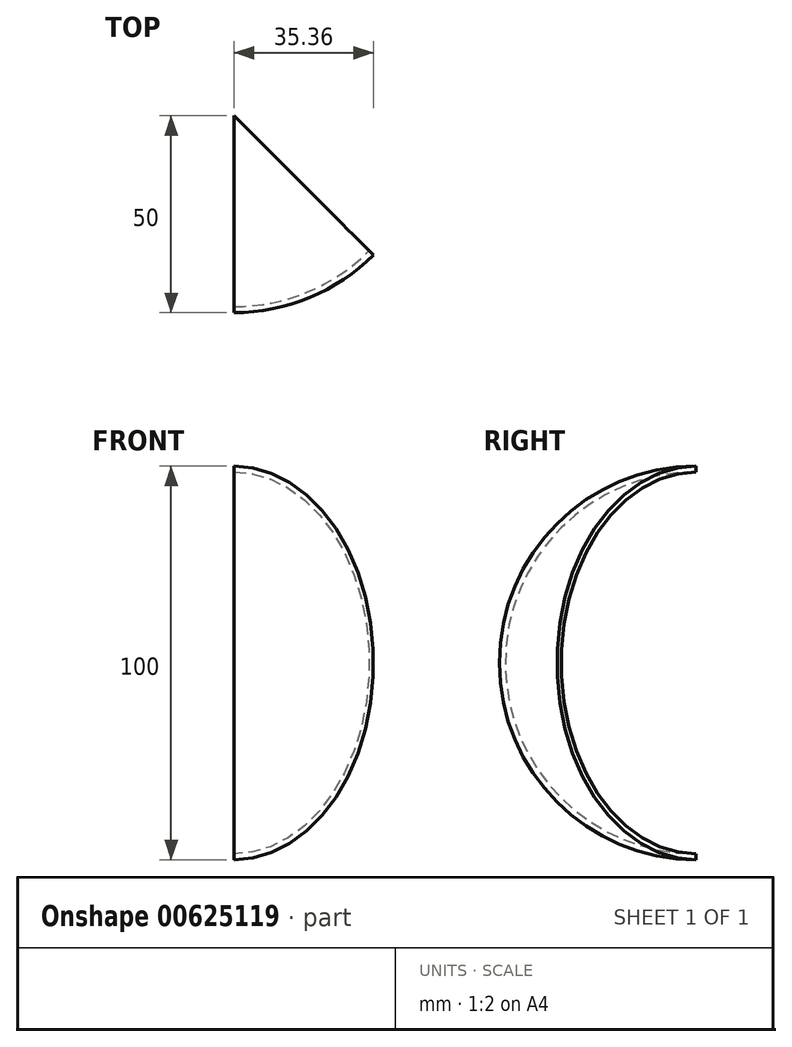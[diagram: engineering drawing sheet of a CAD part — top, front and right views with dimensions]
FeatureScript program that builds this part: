
annotation { "Feature Type Name" : "Feature", "Feature Type Description" : "" }
export const myFeature = defineFeature(function(context is Context, id is Id, definition is map)
    precondition{}
    {
        {
            var Q0;
            Q0=qCreatedBy(makeId("Front.planeOp"),FACE);
            var sketch = newSketch(context, id + "F0", { "sketchPlane" : qUnion([Q0])});
            skArc(sketch, "E0", {"start": v(0, -50) * mm, "mid": v(50, 0) * mm, "end": v(0, 50) * mm});
            skArc(sketch, "E1", {"start": v(0, -48.5) * mm, "mid": v(48.5, 0) * mm, "end": v(0, 48.5) * mm});
            skLineSegment(sketch, "E2", {"start": v(0, 50) * mm, "end": v(0, -50) * mm});
            skSolve(sketch);
        }
        {
            var Q0;
            {var subQ0=sQuery(id+"F0.wireOp",EDGE,"E0");Q0=makeQuery(id+"F0.imprint","IMPRINT",FACE,{"disambiguationData":[TD([[makeQuery(id+"F0.imprint","IMPRINT",EDGE,{"derivedFrom":subQ0}),1.0]])]});}
            var Q1;
            Q1=sQuery(id+"F0.wireOp",EDGE,"E2");
            revolve(context, id + "F1", {"surfaceOperationType" : NewSurfaceOperationType.NEW, "entities" : qUnion([Q0]), "axis" : qUnion([Q1]), "revolveType" : RevolveType.FULL});
        }
        {
            var Q0;
            Q0=qCreatedBy(makeId("Front.planeOp"),FACE);
            var sketch = newSketch(context, id + "F2", { "sketchPlane" : qUnion([Q0])});
            skLineSegment(sketch, "E3.bottom", {"start": v(0, 75.31) * mm, "end": v(-75.26, 75.31) * mm});
            skLineSegment(sketch, "E3.top", {"start": v(0, -74.8) * mm, "end": v(-75.26, -74.8) * mm});
            skLineSegment(sketch, "E3.left", {"start": v(0, 75.31) * mm, "end": v(0, -74.8) * mm});
            skLineSegment(sketch, "E3.right", {"start": v(-75.26, 75.31) * mm, "end": v(-75.26, -74.8) * mm});
            skSolve(sketch);
        }
        {
            var Q0;
            Q0 = qSketchRegion(id + "F2", true);
            extrude(context, id + "F3", {"entities" : qUnion([Q0]), "operationType" : NewBodyOperationType.REMOVE, "endBound" : BoundingType.SYMMETRIC, "depth" : 100 * mm, "offsetDistance" : 25 * mm});
        }
        {
            var Q0;
            Q0=qCreatedBy(makeId("Right.planeOp"),FACE);
            var sketch = newSketch(context, id + "F4", { "sketchPlane" : qUnion([Q0])});
            skLineSegment(sketch, "E4.bottom", {"start": v(0, 75.49) * mm, "end": v(74.84, 75.49) * mm});
            skLineSegment(sketch, "E4.top", {"start": v(0, -74.65) * mm, "end": v(74.84, -74.65) * mm});
            skLineSegment(sketch, "E4.left", {"start": v(0, 75.49) * mm, "end": v(0, -74.65) * mm});
            skLineSegment(sketch, "E4.right", {"start": v(74.84, 75.49) * mm, "end": v(74.84, -74.65) * mm});
            skSolve(sketch);
        }
        {
            var Q0;
            Q0 = qSketchRegion(id + "F4", true);
            extrude(context, id + "F5", {"entities" : qUnion([Q0]), "operationType" : NewBodyOperationType.REMOVE, "endBound" : BoundingType.SYMMETRIC, "depth" : 100 * mm, "offsetDistance" : 25 * mm});
        }
        {
            var Q0;
            Q0=qCreatedBy(makeId("Top.planeOp"),FACE);
            var sketch = newSketch(context, id + "F6", { "sketchPlane" : qUnion([Q0])});
            skLineSegment(sketch, "E5", {"start": v(0, 0) * mm, "end": v(0, -75) * mm});
            skLineSegment(sketch, "E6", {"start": v(0, 0) * mm, "end": v(75, 0) * mm});
            skLineSegment(sketch, "E7", {"start": v(75, 0) * mm, "end": v(75, -75) * mm});
            skLineSegment(sketch, "E8", {"start": v(75, -75) * mm, "end": v(0, 0) * mm});
            skSolve(sketch);
        }
        {
            var Q0;
            Q0 = qSketchRegion(id + "F6", true);
            extrude(context, id + "F7", {"entities" : qUnion([Q0]), "operationType" : NewBodyOperationType.REMOVE, "endBound" : BoundingType.SYMMETRIC, "oppositeDirection" : true, "depth" : 100 * mm, "offsetDistance" : 25 * mm});
        }
    });
